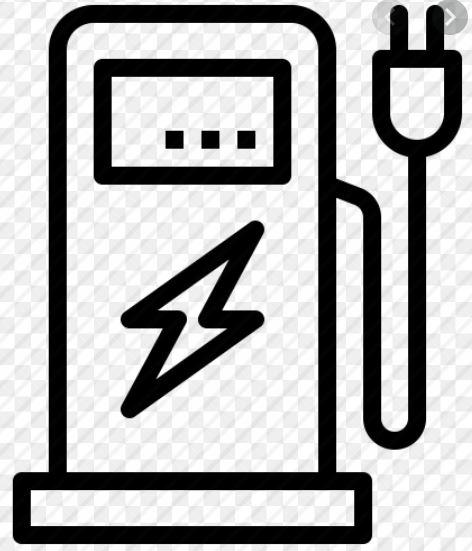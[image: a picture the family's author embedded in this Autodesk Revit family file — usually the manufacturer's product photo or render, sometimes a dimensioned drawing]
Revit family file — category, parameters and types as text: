
# Revit family: Building-ElectricalVehicleCharging-GEWISS-JOINON-ICON_CABLE
name_source: partatom
category: Apparecchi elettrici
units: mm (PartAtom-declared; Revit-internal decimal feet)

## family parameters
Condiviso = No
Host = Superficie
Mantenere orientamento annotazione = Sì
Punto di calcolo locali = Sì
Quota connettore circolare = Usa diametro
Taglio con vuoti quando caricato = No
Tipo di parte = Normale

## types (13) — shared parameters
(Auto)restart electrical protections = Currently not present
BLOCCO = B=C
Colour = Dark grey
Customizations: = Yes (front)
DC Leakage check = Yes
External treatments = No
FORMULA = 1000 mm  [stored 3.28084 ft]
Human Interface = RGB Led
IDF = 4f3378f1-d1c4-4f3c-9264-013b94c6ac45
INPUT: = -
IP degree = IP55
Immagine tipo = ICON_S.jpg
L = 155 mm  [stored 0.50853 ft]
Material = Thermoplastic (Post-industrial origin)
Mechanical characteristics = -
Mouting and installation = Wall mounting (floor mounting with support)
N. of sockets Type 2 = 1
N.poli = 1
OUTPUT : = -
Operating temperature: = -25 +50 °C
POMELLO = bianco
PRESA = Giallo
Produttore = GEWISS S.p.A.
Prospetto di default = 1219 mm
Protection : = DC Leak 6mA
STRUTTURA = RAL - 7035
STRUTTURA ALTA = blue
Shock resistance = IK10
Socket/Connector Nr. (Type) = 1 (Type 2 connector with 5 mt. cable)
Spostamento_S = 1500 mm  [stored 4.92126 ft]
Thermal-magnetic protection = Currently not present
Type of Socket = Type 2 mobile with cable
Type of residual current protection = Currently not present
URL = https://www.gewiss.com
VETRO = Vetro
Version file RFA = 19.4
Voltaggio = 0 V
W = 115 mm  [stored 0.377297 ft]

## per-type parameters (varying)
| type | Charging activation | Charging power | Connectivity: | Current supplied (max): | Descrizione | Energy meter | Max power | Modello | Power meter | RFID | Rated current: | Rated insulation voltage (Ui) | Rated voltage | Terminal blocks: | Total power: |
| GWJ3012W - WB ICON RFID 7 kW T2C IP55 - 4G | Remotely managed, via OCPP 1.6J | 7,4 kW | LAN,4G | 32 Ampere | WB ICON RFID 7 kW T2C IP55 - 4G | YES (MID) | 7,4 Chilowatt | GWJ3012W | YES (MID) | Yes | 32 Ampere | 230 Volt | 230 Volt | 3 x 10 mm² | 7,4 Chilowatt |
| GWJ3113A - WB ICON AUTOSTART DLM 11 kW T2C IP55 | Free access, with dynamic load management | 11 kW | BLE | 16 Ampere | WB ICON AUTOSTART DLM 11 kW T2C IP55 |  | 11 Chilowatt | GWJ3113A | Currently not present |  | 16 Ampere | 400 Volt | 400 Volt | 5 x 10 mm² | 11 Chilowatt |
| GWJ3013A - WB ICON AUTOSTART 11 kW T2C IP55 | Free access | 11 kW | No | 16 Ampere | WB ICON AUTOSTART 11 kW T2C IP55 |  | 11 Chilowatt | GWJ3013A | Currently not present |  | 16 Ampere | 400 Volt | 400 Volt | 5 x 10 mm² | 11 Chilowatt |
| GWJ3014R - WB ICON RFID 22 kW T2C IP55 | Locally managed, via RFID | 22 kW | No | 32 Ampere | WB ICON RFID 22 kW T2C IP55 | No | 22 Chilowatt | GWJ3014R | Currently not present | Yes | 32 Ampere | 400 Volt | 400 Volt | 5 x 10 mm² | 22 Chilowatt |
| GWJ3112A - WB ICON AUTOSTART DLM 7 kW T2C IP55 | Free access, with dynamic load management | 7,4 kW | BLE | 32 Ampere | WB ICON AUTOSTART DLM 7 kW T2C IP55 |  | 7,4 Chilowatt | GWJ3112A | Currently not present |  | 32 Ampere | 230 Volt | 230 Volt | 3 x 10 mm² | 7,4 Chilowatt |
| GWJ3111A - WB ICON AUTOSTART DLM 4 kW T2C IP55 | Free access, with dynamic load management | 4,6 kW | BLE | 20 Ampere | WB ICON AUTOSTART DLM 4 kW T2C IP55 |  | 4,6 Chilowatt | GWJ3111A | Currently not present |  | 20 Ampere | 230 Volt | 230 Volt | 3 x 10 mm² | 4,6 Chilowatt |
| GWJ3014A - WB ICON AUTOSTART 22 kW T2C IP55 | Free access | 22 kW | No | 32 Ampere | WB ICON AUTOSTART 22 kW T2C IP55 |  | 22 Chilowatt | GWJ3014A | Currently not present |  | 32 Ampere | 400 Volt | 400 Volt | 5 x 10 mm² | 22 Chilowatt |
| GWJ3011A - WB ICON AUTOSTART 4 kW T2C IP55 | Free access | 4,6 kW | No | 20 Ampere | WB ICON AUTOSTART 4 kW T2C IP55 |  | 4,6 Chilowatt | GWJ3011A | Currently not present |  | 20 Ampere | 230 Volt | 230 Volt | 3 x 10 mm² | 4,6 Chilowatt |
| GWJ3012R - WB ICON RFID 7 kW T2C IP55 | Locally managed, via RFID | 7,4 kW | No | 32 Ampere | WB ICON RFID 7 kW T2C IP55 | No | 7,4 Chilowatt | GWJ3012R | Currently not present | Yes | 32 Ampere | 230 Volt | 230 Volt | 3 x 10 mm² | 7,4 Chilowatt |
| GWJ3012A - WB ICON AUTOSTART 7 kW T2C IP55 | Free access | 7,4 kW | No | 32 Ampere | WB ICON AUTOSTART 7 kW T2C IP55 |  | 7,4 Chilowatt | GWJ3012A | Currently not present |  | 32 Ampere | 230 Volt | 230 Volt | 3 x 10 mm² | 7,4 Chilowatt |
| GWJ3014W - WB ICON RFID 22 kW T2C IP55 - 4G | Remotely managed, via OCPP 1.6J | 22 kW | LAN,4G | 32 Ampere | WB ICON RFID 22 kW T2C IP55 - 4G | YES (MID) | 22 Chilowatt | GWJ3014W | YES (MID) | Yes | 32 Ampere | 400 Volt | 400 Volt | 5 x 10 mm² | 22 Chilowatt |
| GWJ3012L - WB ICON RFID 7 kW T2C IP55 - ETH | Remotely managed, via OCPP 1.6J | 7,4 kW | LAN | 32 Ampere | WB ICON RFID 7 kW T2C IP55 - ETH | YES (MID) | 7,4 Chilowatt | GWJ3012L | YES (MID) | Yes | 32 Ampere | 230 Volt | 230 Volt | 3 x 10 mm² | 7,4 Chilowatt |
| GWJ3014L - WB ICON RFID 22 kW T2C IP55 - ETH | Remotely managed, via OCPP 1.6J | 22 kW | LAN | 32 Ampere | WB ICON RFID 22 kW T2C IP55 - ETH | YES (MID) | 22 Chilowatt | GWJ3014L | YES (MID) | Yes | 32 Ampere | 400 Volt | 400 Volt | 5 x 10 mm² | 22 Chilowatt |

note: [stored X ft] marks values corroborated as IEEE doubles in the binary element streams (Revit-internal decimal feet)

## geometry (parser evidence)
native form markers: Sweep x3
no freeform markers — native parametric forms only
